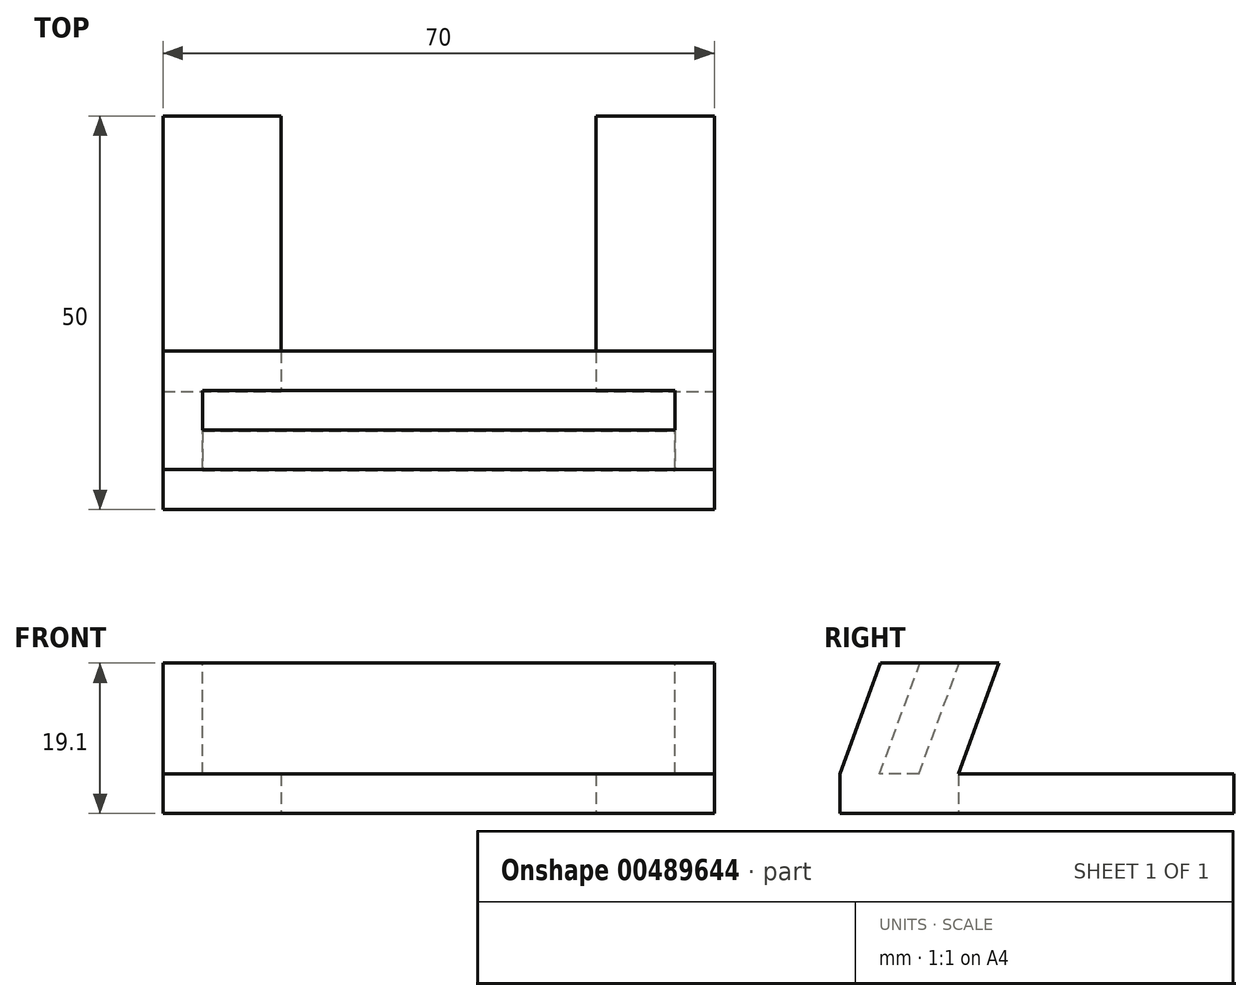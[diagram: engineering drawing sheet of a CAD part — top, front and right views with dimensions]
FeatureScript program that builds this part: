
annotation { "Feature Type Name" : "Feature", "Feature Type Description" : "" }
export const myFeature = defineFeature(function(context is Context, id is Id, definition is map)
    precondition{}
    {
        {
            var Q0;
            Q0=qCreatedBy(makeId("Top.planeOp"),FACE);
            var sketch = newSketch(context, id + "F0", { "sketchPlane" : qUnion([Q0])});
            skLineSegment(sketch, "E0", {"start": v(0, 0) * mm, "end": v(70, 0) * mm});
            skLineSegment(sketch, "E1", {"start": v(70, 0) * mm, "end": v(70, 50) * mm});
            skLineSegment(sketch, "E2", {"start": v(70, 50) * mm, "end": v(55, 50) * mm});
            skLineSegment(sketch, "E3", {"start": v(55, 50) * mm, "end": v(55, 15) * mm});
            skLineSegment(sketch, "E4", {"start": v(55, 15) * mm, "end": v(15, 15) * mm});
            skLineSegment(sketch, "E5", {"start": v(15, 50) * mm, "end": v(0, 50) * mm});
            skLineSegment(sketch, "E6", {"start": v(0, 50) * mm, "end": v(0, 0) * mm});
            skLineSegment(sketch, "E7", {"start": v(15, 50) * mm, "end": v(15, 15) * mm});
            skLineSegment(sketch, "E8", {"start": v(15, 15) * mm, "end": v(15, 0) * mm, "construction": true});
            skSolve(sketch);
        }
        {
            var Q0;
            Q0=makeQuery(id+"F0.imprint","IMPRINT",FACE,{"disambiguationData":[TD([[makeQuery(id+"F0.imprint","IMPRINT",EDGE,{"derivedFrom":sQuery(id+"F0.wireOp",EDGE,"E0")}),1.0]])]});
            extrude(context, id + "F1", {"entities" : qUnion([Q0]), "depth" : 5 * mm});
        }
        {
            var Q0;
            Q0=makeQuery(id+"F1.opExtrude","SWEPT_FACE",FACE,{"disambiguationData":[OSD([sQuery(id+"F0.wireOp",EDGE,"E6")])]});
            var sketch = newSketch(context, id + "F2", { "sketchPlane" : qUnion([Q0])});
            skLineSegment(sketch, "E9", {"start": v(0, 5) * mm, "end": v(-5.13, 19.1) * mm});
            skSolve(sketch);
        }
        {
            var Q0;
            Q0=makeQuery(id+"F1.opExtrude","CAP_FACE",FACE,{"disambiguationData":[OSD([sQuery(id+"F0.wireOp",EDGE,"E0"),sQuery(id+"F0.wireOp",EDGE,"E1"),sQuery(id+"F0.wireOp",EDGE,"E2"),sQuery(id+"F0.wireOp",EDGE,"E3"),sQuery(id+"F0.wireOp",EDGE,"E4"),sQuery(id+"F0.wireOp",EDGE,"E5"),sQuery(id+"F0.wireOp",EDGE,"E6"),sQuery(id+"F0.wireOp",EDGE,"E7")])],"isStart":false});
            var sketch = newSketch(context, id + "F3", { "sketchPlane" : qUnion([Q0])});
            skLineSegment(sketch, "E10.bottom", {"start": v(0, 0) * mm, "end": v(70, 0) * mm});
            skLineSegment(sketch, "E10.top", {"start": v(0, 15) * mm, "end": v(70, 15) * mm});
            skLineSegment(sketch, "E10.left", {"start": v(0, 0) * mm, "end": v(0, 15) * mm});
            skLineSegment(sketch, "E10.right", {"start": v(70, 0) * mm, "end": v(70, 15) * mm});
            skLineSegment(sketch, "E11.bottom", {"start": v(5, 10) * mm, "end": v(65, 10) * mm});
            skLineSegment(sketch, "E11.top", {"start": v(5, 5) * mm, "end": v(65, 5) * mm});
            skLineSegment(sketch, "E11.left", {"start": v(5, 10) * mm, "end": v(5, 5) * mm});
            skLineSegment(sketch, "E11.right", {"start": v(65, 10) * mm, "end": v(65, 5) * mm});
            skPoint(sketch, "E11.middle", {"position": v(35, 7.5) * mm});
            skPoint(sketch, "E11.middle.positionSnap0", {"position": v(0, 7.5) * mm});
            skPoint(sketch, "E11.middle.positionSnap1", {"position": v(35, 15) * mm});
            skPoint(sketch, "E11.centerSnap0", {"position": v(0, 7.5) * mm});
            skPoint(sketch, "E11.centerSnap1", {"position": v(35, 15) * mm});
            skSolve(sketch);
        }
        {
            var Q0;
            Q0 = qSketchRegion(id + "F3", true);
            var Q1;
            Q1 = qConstructionFilter(qBodyType(qCreatedBy(id + "F2" ,EDGE), BodyType.WIRE), ConstructionObject.NO);
            sweep(context, id + "F4", {"operationType" : NewBodyOperationType.ADD, "profiles" : qUnion([Q0]), "path" : qUnion([Q1])});
        }
    });
